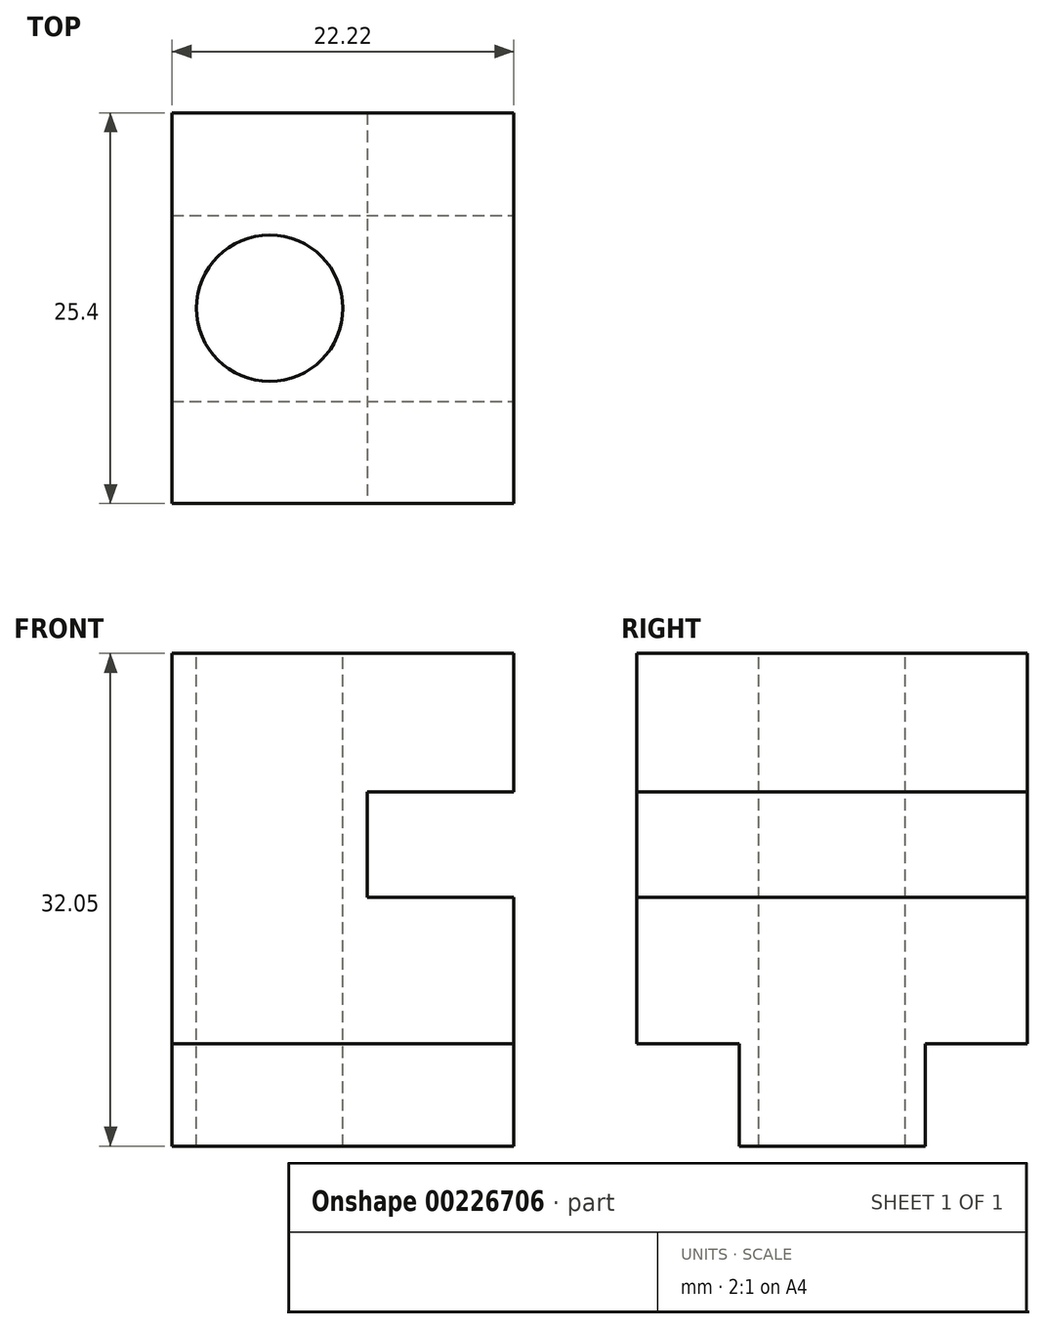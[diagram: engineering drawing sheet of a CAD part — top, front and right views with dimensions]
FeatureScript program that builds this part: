
annotation { "Feature Type Name" : "Feature", "Feature Type Description" : "" }
export const myFeature = defineFeature(function(context is Context, id is Id, definition is map)
    precondition{}
    {
        {
            var Q0;
            Q0=qCreatedBy(makeId("Front.planeOp"),FACE);
            var sketch = newSketch(context, id + "F0", { "sketchPlane" : qUnion([Q0])});
            skLineSegment(sketch, "E0.bottom", {"start": v(11.11, -12.7) * mm, "end": v(-11.11, -12.7) * mm});
            skLineSegment(sketch, "E0.top", {"start": v(11.11, 12.7) * mm, "end": v(-11.11, 12.7) * mm});
            skLineSegment(sketch, "E0.left", {"start": v(11.11, -12.7) * mm, "end": v(11.11, 12.7) * mm});
            skLineSegment(sketch, "E0.right", {"start": v(-11.11, -12.7) * mm, "end": v(-11.11, 12.7) * mm});
            skPoint(sketch, "E0.middle", {"position": v(0, 0) * mm});
            skSolve(sketch);
        }
        {
            var Q0;
            Q0 = qSketchRegion(id + "F0", true);
            extrude(context, id + "F1", {"entities" : qUnion([Q0]), "endBound" : BoundingType.SYMMETRIC, "depth" : 25.4 * mm});
        }
        {
            var Q0;
            Q0=makeQuery(id+"F1.opExtrude","CAP_FACE",FACE,{"disambiguationData":[OSD([sQuery(id+"F0.wireOp",EDGE,"E0.bottom"),sQuery(id+"F0.wireOp",EDGE,"E0.top"),sQuery(id+"F0.wireOp",EDGE,"E0.left"),sQuery(id+"F0.wireOp",EDGE,"E0.right")])],"isStart":false});
            var sketch = newSketch(context, id + "F2", { "sketchPlane" : qUnion([Q0])});
            skLineSegment(sketch, "E1.0", {"start": v(11.11, -12.7) * mm, "end": v(11.11, 12.7) * mm});
            skLineSegment(sketch, "E2.bottom", {"start": v(11.11, 3.68) * mm, "end": v(1.59, 3.68) * mm});
            skLineSegment(sketch, "E2.top", {"start": v(11.11, -3.18) * mm, "end": v(1.59, -3.18) * mm});
            skLineSegment(sketch, "E2.left", {"start": v(11.11, 3.68) * mm, "end": v(11.11, -3.18) * mm});
            skLineSegment(sketch, "E2.right", {"start": v(1.59, 3.68) * mm, "end": v(1.59, -3.18) * mm});
            skSolve(sketch);
        }
        {
            var Q0;
            Q0 = qSketchRegion(id + "F2", true);
            var Q1;
            Q1=makeQuery(id+"F2.imprint","IMPRINT",FACE,{"disambiguationData":[TD([[makeQuery(id+"F2.imprint","IMPRINT",EDGE,{"derivedFrom":sQuery(id+"F2.wireOp",EDGE,"E2.bottom")}),1.0]])]});
            extrude(context, id + "F6", {"entities" : qUnion([Q0, Q1]), "operationType" : NewBodyOperationType.REMOVE, "endBound" : BoundingType.THROUGH_ALL, "oppositeDirection" : true, "depth" : 25.4 * mm});
        }
        {
            var Q0;
            {var subQ0=sQuery(id+"F0.wireOp",EDGE,"E0.bottom");var subQ2=sQuery(id+"F0.wireOp",EDGE,"E0.left");Q0=makeQuery(id+"F6.boolean.opBoolean","SPLIT",FACE,{"disambiguationData":[TD([makeQuery(id+"F1.opExtrude","SWEPT_FACE",FACE,{"disambiguationData":[OSD([subQ0])]})])],"derivedFrom":makeQuery(id+"F1.opExtrude","SWEPT_FACE",FACE,{"disambiguationData":[OSD([subQ2])]})});}
            var sketch = newSketch(context, id + "F7", { "sketchPlane" : qUnion([Q0])});
            skLineSegment(sketch, "E3.bottom", {"start": v(-6.05, -12.7) * mm, "end": v(6.05, -12.7) * mm});
            skLineSegment(sketch, "E3.top", {"start": v(-6.05, -19.35) * mm, "end": v(6.05, -19.35) * mm});
            skLineSegment(sketch, "E3.left", {"start": v(-6.05, -12.7) * mm, "end": v(-6.05, -19.35) * mm});
            skLineSegment(sketch, "E3.right", {"start": v(6.05, -12.7) * mm, "end": v(6.05, -19.35) * mm});
            skLineSegment(sketch, "E4.0", {"start": v(12.7, -3.17) * mm, "end": v(-12.7, -3.17) * mm});
            skPoint(sketch, "E5.0", {"position": v(0, 0) * mm});
            skPoint(sketch, "E6", {"position": v(0, -19.35) * mm});
            skSolve(sketch);
        }
        {
            var Q0;
            Q0 = qSketchRegion(id + "F7", true);
            var Q1;
            Q1=makeQuery(id+"F1.opExtrude","SWEPT_FACE",FACE,{"disambiguationData":[OSD([sQuery(id+"F0.wireOp",EDGE,"E0.right")])]});
            extrude(context, id + "F3", {"entities" : qUnion([Q0]), "operationType" : NewBodyOperationType.ADD, "endBound" : BoundingType.UP_TO_SURFACE, "oppositeDirection" : true, "endBoundEntityFace" : qUnion([Q1]), "depth" : 25.4 * mm});
        }
        {
            var Q0;
            Q0=makeQuery(id+"F1.opExtrude","SWEPT_FACE",FACE,{"disambiguationData":[OSD([sQuery(id+"F0.wireOp",EDGE,"E0.top")])]});
            var sketch = newSketch(context, id + "F8", { "sketchPlane" : qUnion([Q0])});
            skLineSegment(sketch, "E7.0", {"start": v(1.59, 12.7) * mm, "end": v(1.59, -12.7) * mm});
            skCircle(sketch, "E8", {"center": v(-4.76, 0) * mm, "radius": 4.76 * mm});
            skPoint(sketch, "E8.centerSnap0", {"position": v(1.59, 0) * mm});
            skLineSegment(sketch, "E9", {"start": v(1.59, 0) * mm, "end": v(-11.11, 0) * mm});
            skSolve(sketch);
        }
        {
            var Q0;
            Q0 = qSketchRegion(id + "F8", true);
            extrude(context, id + "F4", {"entities" : qUnion([Q0]), "operationType" : NewBodyOperationType.REMOVE, "endBound" : BoundingType.THROUGH_ALL, "oppositeDirection" : true, "depth" : 25.4 * mm});
        }
    });
